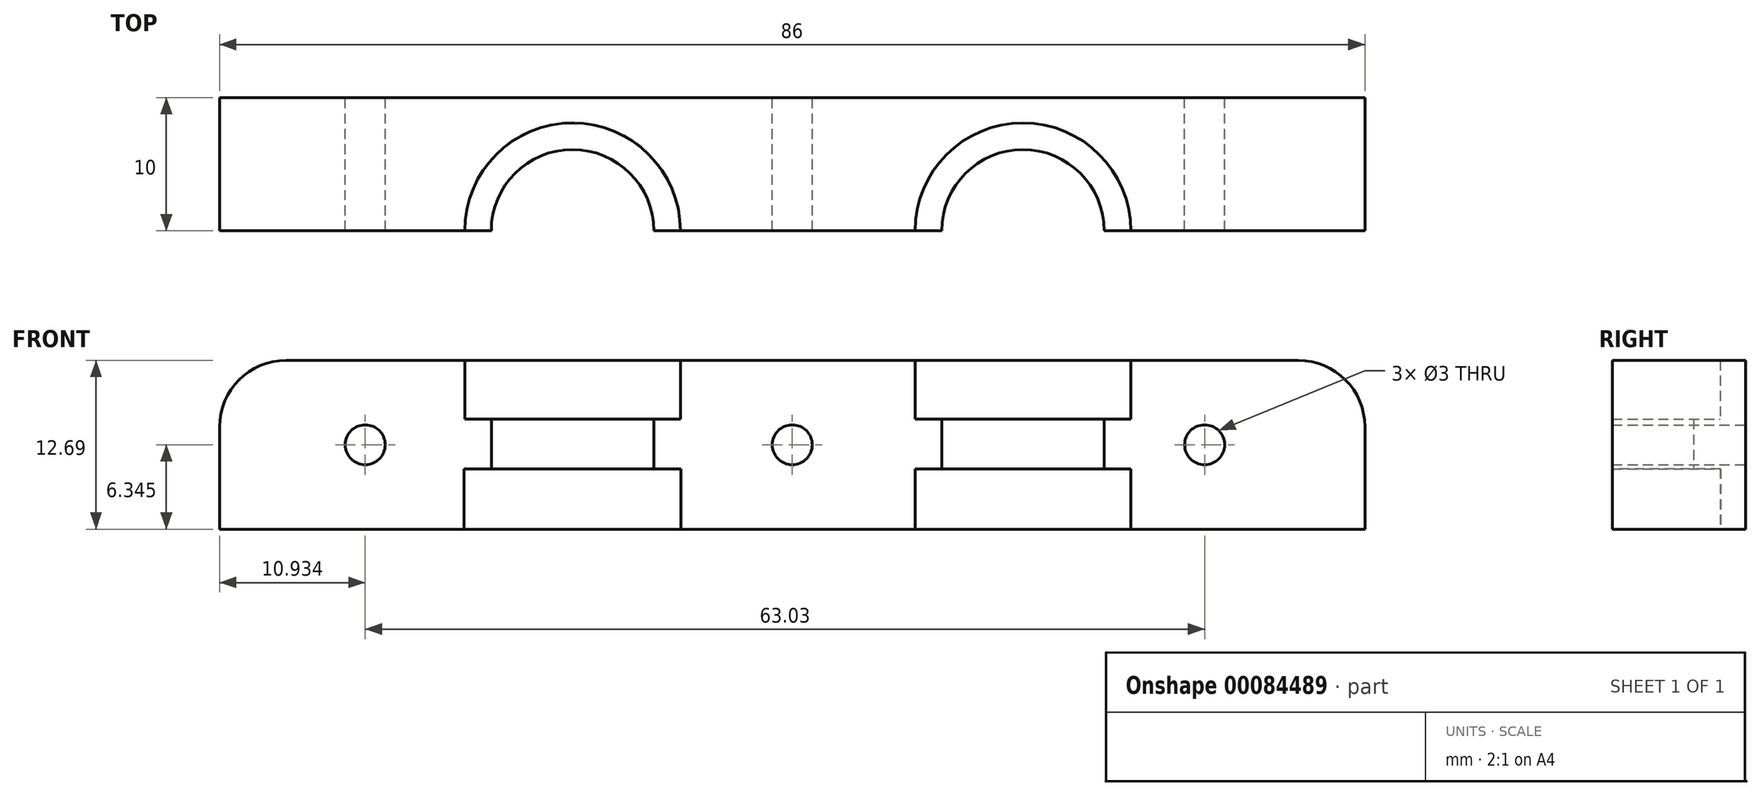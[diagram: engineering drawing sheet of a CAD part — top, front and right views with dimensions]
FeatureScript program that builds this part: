
annotation { "Feature Type Name" : "Feature", "Feature Type Description" : "" }
export const myFeature = defineFeature(function(context is Context, id is Id, definition is map)
    precondition{}
    {
        {
            var Q0;
            Q0=qCreatedBy(makeId("Top.planeOp"),FACE);
            var sketch = newSketch(context, id + "F0", { "sketchPlane" : qUnion([Q0])});
            skLineSegment(sketch, "E0.bottom", {"start": v(-43, 5) * mm, "end": v(43, 5) * mm});
            skLineSegment(sketch, "E0.top", {"start": v(-43, -5) * mm, "end": v(43, -5) * mm});
            skLineSegment(sketch, "E0.left", {"start": v(-43, 5) * mm, "end": v(-43, -5) * mm});
            skLineSegment(sketch, "E0.right", {"start": v(43, 5) * mm, "end": v(43, -5) * mm});
            skPoint(sketch, "E0.middle", {"position": v(0, 0) * mm});
            skSolve(sketch);
        }
        {
            var Q0;
            Q0=makeQuery(id+"F0.imprint","IMPRINT",FACE,{"disambiguationData":[TD([[makeQuery(id+"F0.imprint","IMPRINT",EDGE,{"derivedFrom":sQuery(id+"F0.wireOp",EDGE,"E0.bottom")}),-1.0]])]});
            var Q1;
            Q1 = qSketchRegion(id + "F2", true);
            extrude(context, id + "F1", {"entities" : qUnion([Q0, Q1]), "depth" : 12.7 * mm});
        }
        {
            var Q0;
            Q0=makeQuery(id+"F1.opExtrude","SWEPT_FACE",FACE,{"disambiguationData":[OSD([sQuery(id+"F0.wireOp",EDGE,"E0.top")])]});
            var sketch = newSketch(context, id + "F2", { "sketchPlane" : qUnion([Q0])});
            skLineSegment(sketch, "E1.bottom", {"start": v(-16.5, 12.7) * mm, "end": v(16.5, 12.7) * mm, "construction": true});
            skLineSegment(sketch, "E1.top", {"start": v(-16.5, 0) * mm, "end": v(16.5, 0) * mm, "construction": true});
            skLineSegment(sketch, "E1.left", {"start": v(-16.5, 12.7) * mm, "end": v(-16.5, 0) * mm, "construction": true});
            skLineSegment(sketch, "E1.right", {"start": v(16.5, 12.7) * mm, "end": v(16.5, 0) * mm, "construction": true});
            skLineSegment(sketch, "E2", {"start": v(0, 0) * mm, "end": v(0, 16.48) * mm, "construction": true});
            skLineSegment(sketch, "E3.bottom", {"start": v(-16.5, 12.7) * mm, "end": v(-8.4, 12.7) * mm});
            skLineSegment(sketch, "E3.top", {"start": v(-16.5, 0) * mm, "end": v(-8.36, 0) * mm});
            skLineSegment(sketch, "E3.left", {"start": v(-16.5, 12.7) * mm, "end": v(-16.5, 0) * mm});
            skLineSegment(sketch, "E4.bottom", {"start": v(-16.5, 8.26) * mm, "end": v(-10.4, 8.26) * mm});
            skLineSegment(sketch, "E4.top", {"start": v(-16.5, 4.54) * mm, "end": v(-10.4, 4.54) * mm});
            skLineSegment(sketch, "E4.left", {"start": v(-16.5, 8.26) * mm, "end": v(-16.5, 4.54) * mm});
            skLineSegment(sketch, "E4.right", {"start": v(-10.4, 8.26) * mm, "end": v(-10.4, 4.54) * mm});
            skLineSegment(sketch, "E5", {"start": v(-10.4, 8.26) * mm, "end": v(-8.4, 8.26) * mm});
            skLineSegment(sketch, "E6", {"start": v(-8.36, 4.54) * mm, "end": v(-10.4, 4.54) * mm});
            skLineSegment(sketch, "E7.trimOffspring", {"start": v(-8.36, 4.54) * mm, "end": v(-8.36, 0) * mm});
            skLineSegment(sketch, "E8", {"start": v(-8.4, 12.7) * mm, "end": v(-8.4, 8.26) * mm});
            skSolve(sketch);
        }
        {
            var Q0;
            Q0 = qSketchRegion(id + "F2", true);
            var Q1;
            Q1=sQuery(id+"F2.wireOp",EDGE,"E3.left");
            revolve(context, id + "F3", {"operationType" : NewBodyOperationType.REMOVE, "entities" : qUnion([Q0]), "axis" : qUnion([Q1]), "revolveType" : RevolveType.FULL, "oppositeDirection" : true});
        }
        {
            var Q0;
            {var subQ0=sQuery(id+"F0.wireOp",EDGE,"E0.right");var subQ2=sQuery(id+"F0.wireOp",EDGE,"E0.top");Q0=makeQuery(id+"F3.boolean.opBoolean","SPLIT",FACE,{"disambiguationData":[TD([makeQuery(id+"F1.opExtrude","SWEPT_FACE",FACE,{"disambiguationData":[OSD([subQ0])]})])],"derivedFrom":makeQuery(id+"F1.opExtrude","SWEPT_FACE",FACE,{"disambiguationData":[OSD([subQ2])]})});}
            var sketch = newSketch(context, id + "F4", { "sketchPlane" : qUnion([Q0])});
            skLineSegment(sketch, "E9.bottom", {"start": v(43, 12.7) * mm, "end": v(-8.36, 12.69) * mm, "construction": true});
            skLineSegment(sketch, "E9.top", {"start": v(43, 0) * mm, "end": v(-8.36, 0) * mm, "construction": true});
            skLineSegment(sketch, "E9.left", {"start": v(43, 12.7) * mm, "end": v(43, 0) * mm, "construction": true});
            skLineSegment(sketch, "E9.right", {"start": v(-8.36, 12.7) * mm, "end": v(-8.36, 0) * mm, "construction": true});
            skLineSegment(sketch, "E10", {"start": v(17.32, 0) * mm, "end": v(17.32, 12.69) * mm, "construction": true});
            skLineSegment(sketch, "E11.bottom", {"start": v(17.32, 12.69) * mm, "end": v(25.42, 12.69) * mm});
            skLineSegment(sketch, "E11.top", {"start": v(17.32, 0) * mm, "end": v(25.42, 0) * mm});
            skLineSegment(sketch, "E11.left", {"start": v(17.32, 12.69) * mm, "end": v(17.32, 0) * mm});
            skLineSegment(sketch, "E11.right", {"start": v(25.42, 12.69) * mm, "end": v(25.42, 8.26) * mm});
            skLineSegment(sketch, "E12.bottom", {"start": v(17.32, 8.26) * mm, "end": v(23.42, 8.26) * mm});
            skLineSegment(sketch, "E12.top", {"start": v(17.32, 4.54) * mm, "end": v(23.42, 4.54) * mm});
            skLineSegment(sketch, "E12.left", {"start": v(17.32, 8.26) * mm, "end": v(17.32, 4.54) * mm});
            skLineSegment(sketch, "E12.right", {"start": v(23.42, 8.26) * mm, "end": v(23.42, 4.54) * mm});
            skLineSegment(sketch, "E13", {"start": v(23.42, 8.26) * mm, "end": v(25.42, 8.26) * mm});
            skLineSegment(sketch, "E14", {"start": v(25.42, 4.54) * mm, "end": v(23.42, 4.54) * mm});
            skLineSegment(sketch, "E15.trimOffspring", {"start": v(25.42, 4.54) * mm, "end": v(25.42, 0) * mm});
            skSolve(sketch);
        }
        {
            var Q0;
            Q0 = qSketchRegion(id + "F4", true);
            var Q1;
            Q1=sQuery(id+"F4.wireOp",EDGE,"E11.left");
            revolve(context, id + "F5", {"operationType" : NewBodyOperationType.REMOVE, "entities" : qUnion([Q0]), "axis" : qUnion([Q1]), "revolveType" : RevolveType.FULL, "oppositeDirection" : true});
        }
        {
            var Q0;
            Q0=makeQuery(id+"F1.opExtrude","CAP_EDGE",EDGE,{"disambiguationData":[OSD([sQuery(id+"F0.wireOp",EDGE,"E0.left")])],"isStart":false});
            var Q1;
            Q1=makeQuery(id+"F1.opExtrude","CAP_EDGE",EDGE,{"disambiguationData":[OSD([sQuery(id+"F0.wireOp",EDGE,"E0.right")])],"isStart":false});
            fillet(context, id + "F6", {"entities" : qUnion([Q0, Q1]), "radius" : 5 * mm, "tangentPropagation" : true, "allowEdgeOverflow" : false});
        }
        {
            var Q0;
            Q0=makeQuery(id+"F1.opExtrude","SWEPT_FACE",FACE,{"disambiguationData":[OSD([sQuery(id+"F0.wireOp",EDGE,"E0.bottom")])]});
            var sketch = newSketch(context, id + "F7", { "sketchPlane" : qUnion([Q0])});
            skLineSegment(sketch, "E16.bottom", {"start": v(-43, 0) * mm, "end": v(43, 0) * mm, "construction": true});
            skLineSegment(sketch, "E16.top", {"start": v(-43, 12.7) * mm, "end": v(43, 12.7) * mm, "construction": true});
            skLineSegment(sketch, "E16.left", {"start": v(-43, 0) * mm, "end": v(-43, 12.7) * mm, "construction": true});
            skLineSegment(sketch, "E16.right", {"start": v(43, 0) * mm, "end": v(43, 12.7) * mm, "construction": true});
            skLineSegment(sketch, "E17", {"start": v(0, 0) * mm, "end": v(0, 12.7) * mm, "construction": true});
            skLineSegment(sketch, "E18", {"start": v(-43, 6.34) * mm, "end": v(43, 6.34) * mm, "construction": true});
            skCircle(sketch, "E19", {"center": v(-30.96, 6.34) * mm, "radius": 1.5 * mm});
            skCircle(sketch, "E20", {"center": v(0, 6.34) * mm, "radius": 1.5 * mm});
            skCircle(sketch, "E21", {"center": v(32.07, 6.34) * mm, "radius": 1.5 * mm});
            skSolve(sketch);
        }
        {
            var Q0;
            Q0=makeQuery(id+"F7.imprint","IMPRINT",FACE,{"disambiguationData":[TD([[makeQuery(id+"F7.imprint","IMPRINT",EDGE,{"derivedFrom":sQuery(id+"F7.wireOp",EDGE,"E19")}),1.0]])]});
            var Q1;
            Q1=makeQuery(id+"F7.imprint","IMPRINT",FACE,{"disambiguationData":[TD([[makeQuery(id+"F7.imprint","IMPRINT",EDGE,{"derivedFrom":sQuery(id+"F7.wireOp",EDGE,"E20")}),1.0]])]});
            var Q2;
            Q2=makeQuery(id+"F7.imprint","IMPRINT",FACE,{"disambiguationData":[TD([[makeQuery(id+"F7.imprint","IMPRINT",EDGE,{"derivedFrom":sQuery(id+"F7.wireOp",EDGE,"E21")}),1.0]])]});
            extrude(context, id + "F8", {"entities" : qUnion([Q0, Q1, Q2]), "operationType" : NewBodyOperationType.REMOVE, "endBound" : BoundingType.THROUGH_ALL, "oppositeDirection" : true, "depth" : 25 * mm});
        }
    });
